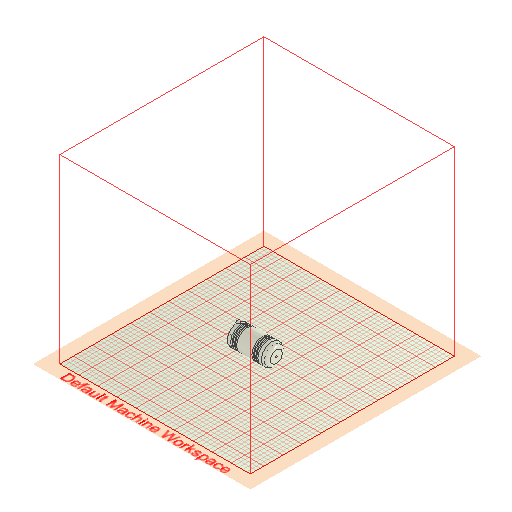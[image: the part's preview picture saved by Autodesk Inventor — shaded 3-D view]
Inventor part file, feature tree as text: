
AUTODESK INVENTOR PART (.ipt)
format: ipt  version: 2022.1 (Build 261234020, 234B)  size: 629,760 bytes
history: native  units: mm
features: extrude x24, sketch x8, fillet x4, other x3, projected_geometry x2
ambient origin geometry x8: Origin, YZ Plane, XZ Plane, XY Plane, X Axis, Y Axis, Z Axis, Center Point
bodies: Solid1 (feature_tree)
feature tree (41):
  other  "Table"
  other  "Carcasa V3-01"
  sketch  "Sketch1"  dims[d0=47.0mm d1=42.0mm]
  extrude  "Extrusion1"  Depth=42.0mm
  extrude  "Extrusion2"  Depth=10.0mm TaperAngle=0.0deg
  fillet  "Fillet1"  Radius=10.0mm
  extrude  "Extrusion3"  Depth=40.0mm TaperAngle=0.0deg
  extrude  "Extrusion4"  Depth=8.0mm
  extrude  "Extrusion5"  Depth=10.0mm
  extrude  "Extrusion6"  Depth=4.0mm
  extrude  "Extrusion7"  Depth=1.0mm
  other  "Lip1"
  extrude  "Extrusion10"  Depth=1.0mm TaperAngle=0.0deg
  extrude  "Extrusion11"  Depth=1.0mm
  sketch  "Sketch8"  dims[d17=100.0mm d18=0.0mm]
  extrude  "Extrusion12"  Depth=1.0mm TaperAngle=0.0deg
  extrude  "Extrusion13"  Depth=1.0mm TaperAngle=0.0deg
  extrude  "Extrusion14"  Depth=1.0mm TaperAngle=0.0deg
  extrude  "Extrusion15"  Depth=1.0mm TaperAngle=0.0deg
  extrude  "Extrusion16"  Depth=1.0mm TaperAngle=0.0deg
  extrude  "Extrusion17"  Depth=1.0mm TaperAngle=0.0deg
  fillet  "Fillet2"  Radius=3.0mm
  extrude  "Extrusion18"  Depth=1.0mm TaperAngle=0.0deg
  extrude  "Extrusion19"  Depth=1.0mm TaperAngle=0.0deg
  extrude  "Extrusion20"  Depth=1.0mm TaperAngle=0.0deg
  extrude  "Extrusion21"  Depth=1.0mm TaperAngle=0.0deg
  extrude  "Extrusion22"  Depth=1.0mm TaperAngle=0.0deg
  extrude  "Extrusion23"  Depth=1.0mm TaperAngle=0.0deg
  fillet  "Fillet3"  Radius=3.0mm
  extrude  "Extrusion25"  Depth=1.0mm
  sketch  "Sketch15"  dims[d34=30.0mm d35=0.0mm d36=5.0mm d37=30.0mm d38=0.0mm d39=49.0mm d40=67.5mm d41=0.0mm d42=64.5mm d43=0.0mm d44=62.5mm d45=0.0mm d46=59.5mm d47=0.0mm d48=57.5mm d49=0.0mm d50=54.5mm d51=0.0mm d52=3.0mm d53=20.5mm d54=0.0mm d55=17.5mm d56=0.0mm d57=15.5mm d58=0.0mm d59=12.5mm d60=0.0mm d61=10.5mm d62=0.0mm d63=7.5mm d64=0.0mm d65=3.0mm d132=6.0mm d133=6.0mm d134=1.0mm d135=0.0mm d136=4.5mm d144=10.0mm d145=0.0mm d146=10.0mm d147=0.0mm d148=28.0mm d149=8.0mm d150=2.5mm d151=5.5mm d152=28.0mm d153=8.0mm d154=5.5mm d155=2.5mm d156=1.0mm d71=0.872665mm d72=0.872665mm d81=0.0mm d82=0.0mm d83=0.0mm d84=0.0mm]
  extrude  "Extrusion26"  Depth=1.0mm
  extrude  "Extrusion27"  Depth=1.0mm TaperAngle=0.0deg
  fillet  "Fillet5"  Radius=4.5mm
  sketch  "Sketch2"  dims[d2=100.0mm d3=0.0mm d4=95.0mm d5=0.0mm d6=10.0mm]
  sketch  "Sketch3"  dims[d7=55.0mm d8=0.0mm d9=40.0mm d10=0.0mm]
  projected_geometry  "Projected Loop1"
  sketch  "Sketch6"  dims[d11=1.0mm d12=0.0mm d13=8.0mm]
  sketch  "Sketch7"  dims[d14=10.0mm d15=0.0mm d16=15.0mm]
  projected_geometry  "Projected Loop2"
  sketch  "Sketch13"  dims[d19=3.0mm d20=1.5mm d21=0.0mm d22=0.0mm d23=0.872665mm d24=0.0mm d33=4.0mm]
